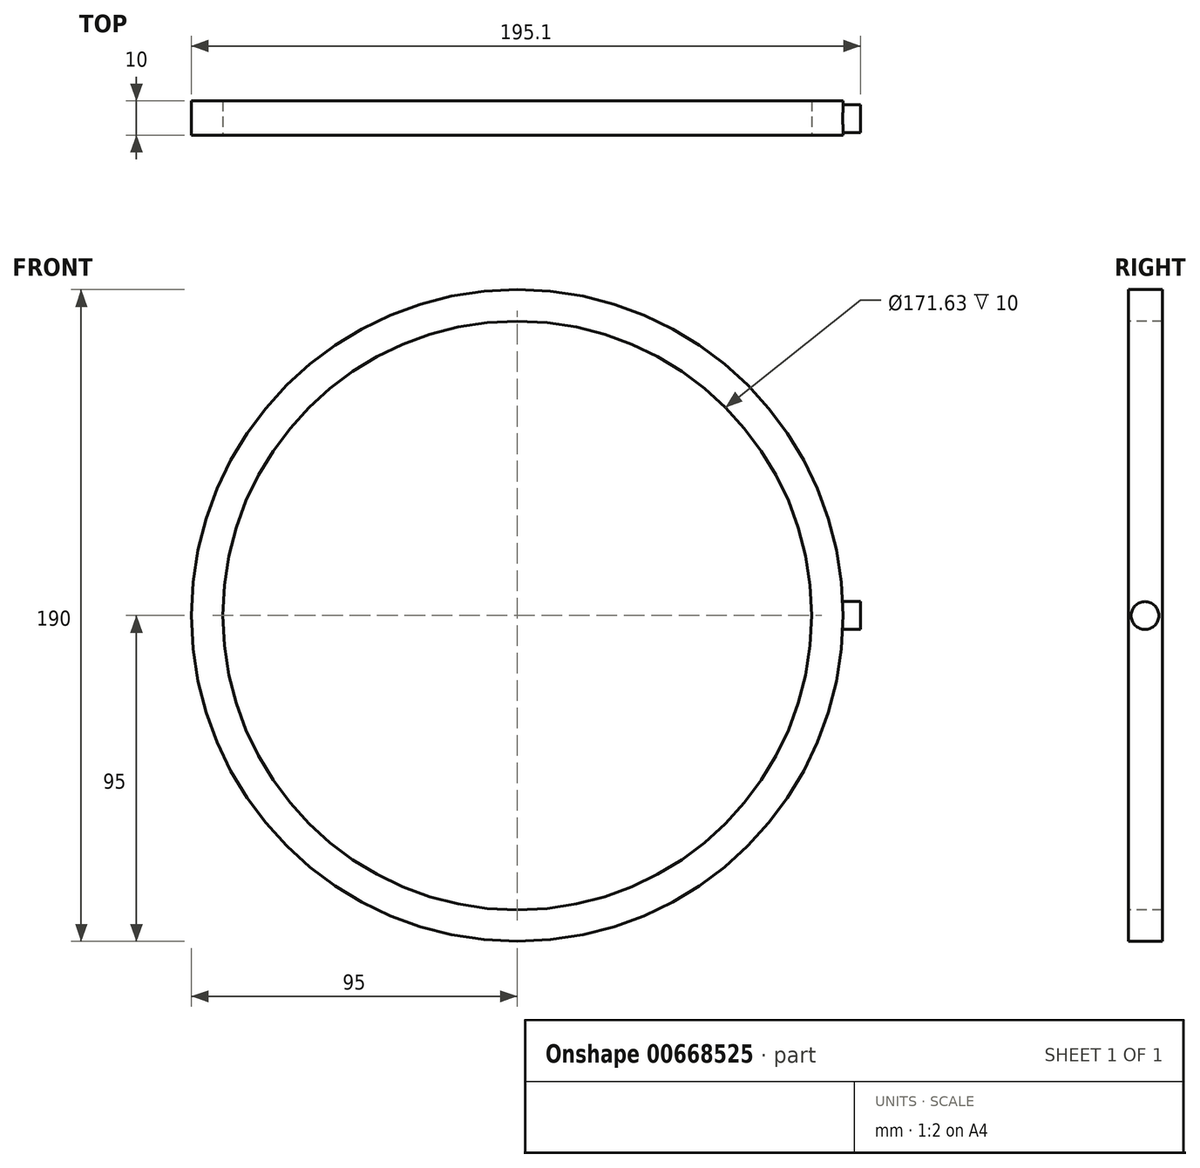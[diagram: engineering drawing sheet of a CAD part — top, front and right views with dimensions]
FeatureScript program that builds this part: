
annotation { "Feature Type Name" : "Feature", "Feature Type Description" : "" }
export const myFeature = defineFeature(function(context is Context, id is Id, definition is map)
    precondition{}
    {
        {
            var Q0;
            Q0=qCreatedBy(makeId("Front.planeOp"),FACE);
            var sketch = newSketch(context, id + "F0", { "sketchPlane" : qUnion([Q0])});
            skCircle(sketch, "E0", {"center": v(0, 0) * mm, "radius": 95 * mm});
            skSolve(sketch);
        }
        {
            var Q0;
            Q0=makeQuery(id+"F0.imprint","IMPRINT",FACE,{"disambiguationData":[TD([[makeQuery(id+"F0.imprint","IMPRINT",EDGE,{"derivedFrom":sQuery(id+"F0.wireOp",EDGE,"E0")}),1.0]])]});
            extrude(context, id + "F1", {"entities" : qUnion([Q0]), "depth" : 10 * mm, "offsetDistance" : 25 * mm});
        }
        {
            var Q0;
            Q0=makeQuery(id+"F1.opExtrude","CAP_FACE",FACE,{"disambiguationData":[OSD([sQuery(id+"F0.wireOp",EDGE,"E0")])],"isStart":false});
            var sketch = newSketch(context, id + "F2", { "sketchPlane" : qUnion([Q0])});
            skCircle(sketch, "E1", {"center": v(0, 0) * mm, "radius": 85.81 * mm});
            skSolve(sketch);
        }
        {
            var Q0;
            Q0=makeQuery(id+"F2.imprint","IMPRINT",FACE,{"disambiguationData":[TD([[makeQuery(id+"F2.imprint","IMPRINT",EDGE,{"derivedFrom":sQuery(id+"F2.wireOp",EDGE,"E1")}),1.0]])]});
            extrude(context, id + "F3", {"entities" : qUnion([Q0]), "operationType" : NewBodyOperationType.REMOVE, "oppositeDirection" : true, "depth" : 25 * mm, "offsetDistance" : 25 * mm});
        }
        {
            var Q0;
            Q0=qCreatedBy(makeId("Right.planeOp"),FACE);
            cPlane(context, id + "F4", {"entities" : qUnion([Q0]), "cplaneType" : CPlaneType.OFFSET, "offset" : 90.1 * mm, "width" : 150 * mm, "height" : 150 * mm});
        }
        {
            var Q0;
            Q0=qCreatedBy(id+"F4.planeOp",FACE);
            var sketch = newSketch(context, id + "F5", { "sketchPlane" : qUnion([Q0])});
            skCircle(sketch, "E2", {"center": v(-5.13, 0) * mm, "radius": 4.05 * mm});
            skSolve(sketch);
        }
        {
            var Q0;
            Q0 = qSketchRegion(id + "F5", true);
            extrude(context, id + "F6", {"entities" : qUnion([Q0]), "operationType" : NewBodyOperationType.ADD, "depth" : 10 * mm, "offsetDistance" : 25 * mm});
        }
    });
